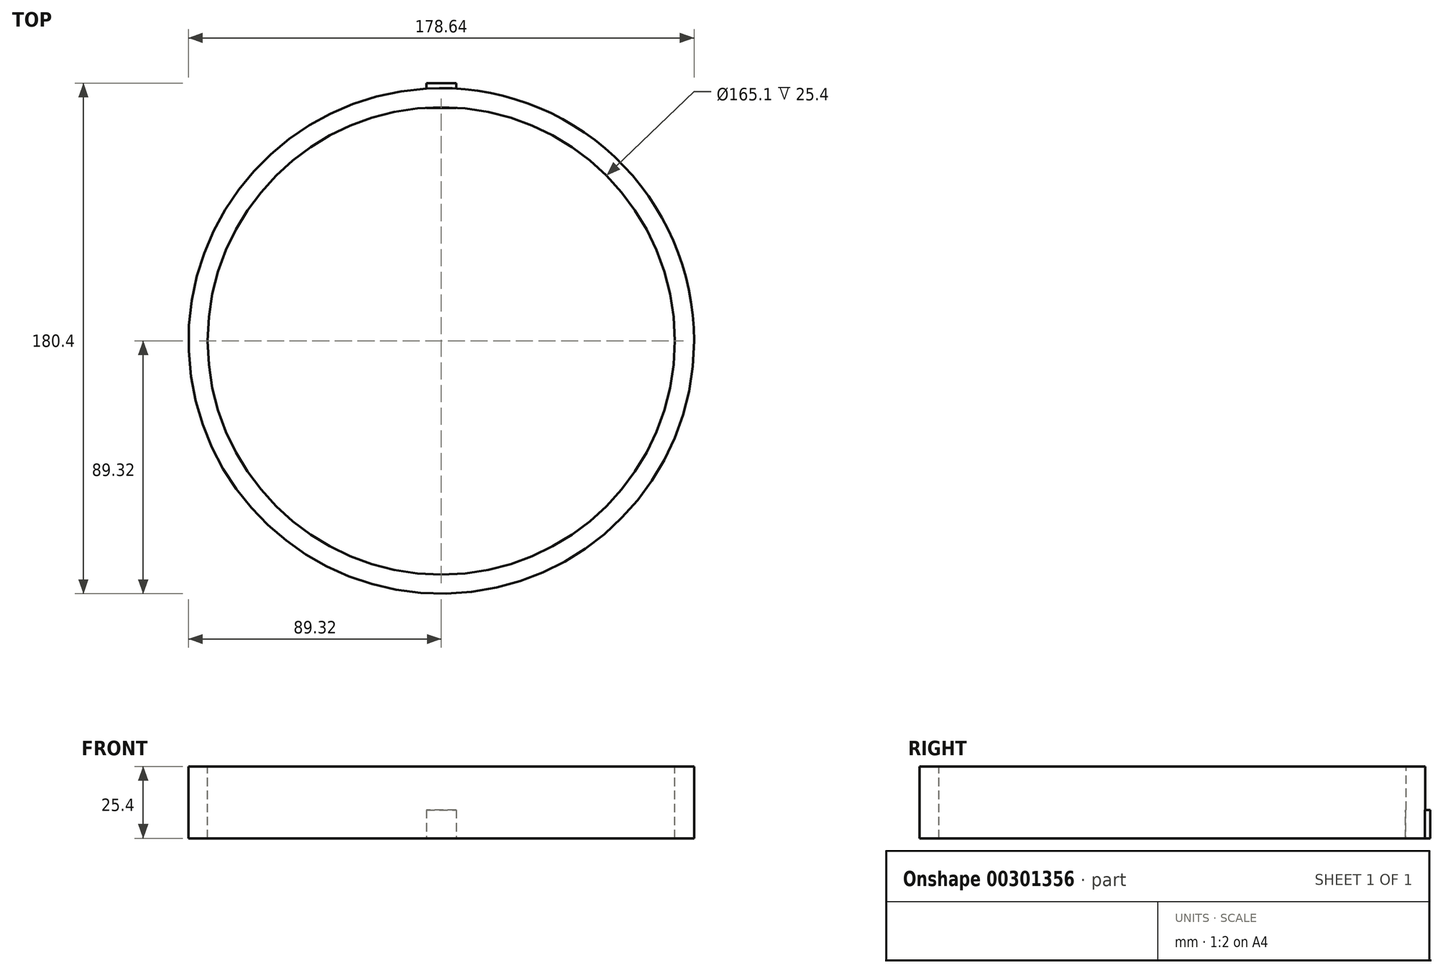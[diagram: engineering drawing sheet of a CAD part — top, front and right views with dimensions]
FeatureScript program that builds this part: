
annotation { "Feature Type Name" : "Feature", "Feature Type Description" : "" }
export const myFeature = defineFeature(function(context is Context, id is Id, definition is map)
    precondition{}
    {
        {
            var Q0;
            Q0=qCreatedBy(makeId("Top.planeOp"),FACE);
            var sketch = newSketch(context, id + "F0", { "sketchPlane" : qUnion([Q0])});
            skCircle(sketch, "E0", {"center": v(0, 0) * mm, "radius": 89.32 * mm});
            skSolve(sketch);
        }
        {
            var Q0;
            Q0 = qSketchRegion(id + "F0", true);
            extrude(context, id + "F1", {"entities" : qUnion([Q0]), "depth" : 25.4 * mm});
        }
        {
            var Q0;
            Q0=makeQuery(id+"F1.opExtrude","CAP_FACE",FACE,{"disambiguationData":[OSD([sQuery(id+"F0.wireOp",EDGE,"E0")])],"isStart":false});
            var sketch = newSketch(context, id + "F2", { "sketchPlane" : qUnion([Q0])});
            skCircle(sketch, "E1", {"center": v(0, 0) * mm, "radius": 83.77 * mm});
            skSolve(sketch);
        }
        {
            var Q0;
            Q0=sQuery(id+"F2.wireOp",VERTEX,"E1.center");
            var Q1;
            Q1=makeQuery(id+"F1.opExtrude","SWEPT_BODY",BODY,{"disambiguationData":[OSD([sQuery(id+"F0.wireOp",EDGE,"E0")])]});
            hole(context, id + "F3", {"style" : HoleStyle.SIMPLE, "endStyle" : HoleEndStyle.BLIND, "holeDiameter" : 165.1 * mm, "holeDepth" : 101.6 * mm, "tappedDepth" : 12.7 * mm, "tapClearance" : 3, "startFromSketch" : true, "locations" : qUnion([Q0]), "scope" : qUnion([Q1])});
        }
        {
            var Q0;
            Q0=qCreatedBy(makeId("Top.planeOp"),FACE);
            var sketch = newSketch(context, id + "F4", { "sketchPlane" : qUnion([Q0])});
            skLineSegment(sketch, "E2.bottom", {"start": v(-5.3, 91.08) * mm, "end": v(5.3, 91.08) * mm});
            skLineSegment(sketch, "E2.top", {"start": v(-5.3, 82.3) * mm, "end": v(5.3, 82.3) * mm});
            skLineSegment(sketch, "E2.left", {"start": v(-5.3, 91.08) * mm, "end": v(-5.3, 82.3) * mm});
            skLineSegment(sketch, "E2.right", {"start": v(5.3, 91.08) * mm, "end": v(5.3, 82.3) * mm});
            skPoint(sketch, "E2.middle", {"position": v(0, 86.69) * mm});
            skSolve(sketch);
        }
        {
            var Q0;
            Q0 = qSketchRegion(id + "F4", true);
            extrude(context, id + "F5", {"entities" : qUnion([Q0]), "operationType" : NewBodyOperationType.ADD, "depth" : 10 * mm});
        }
    });
